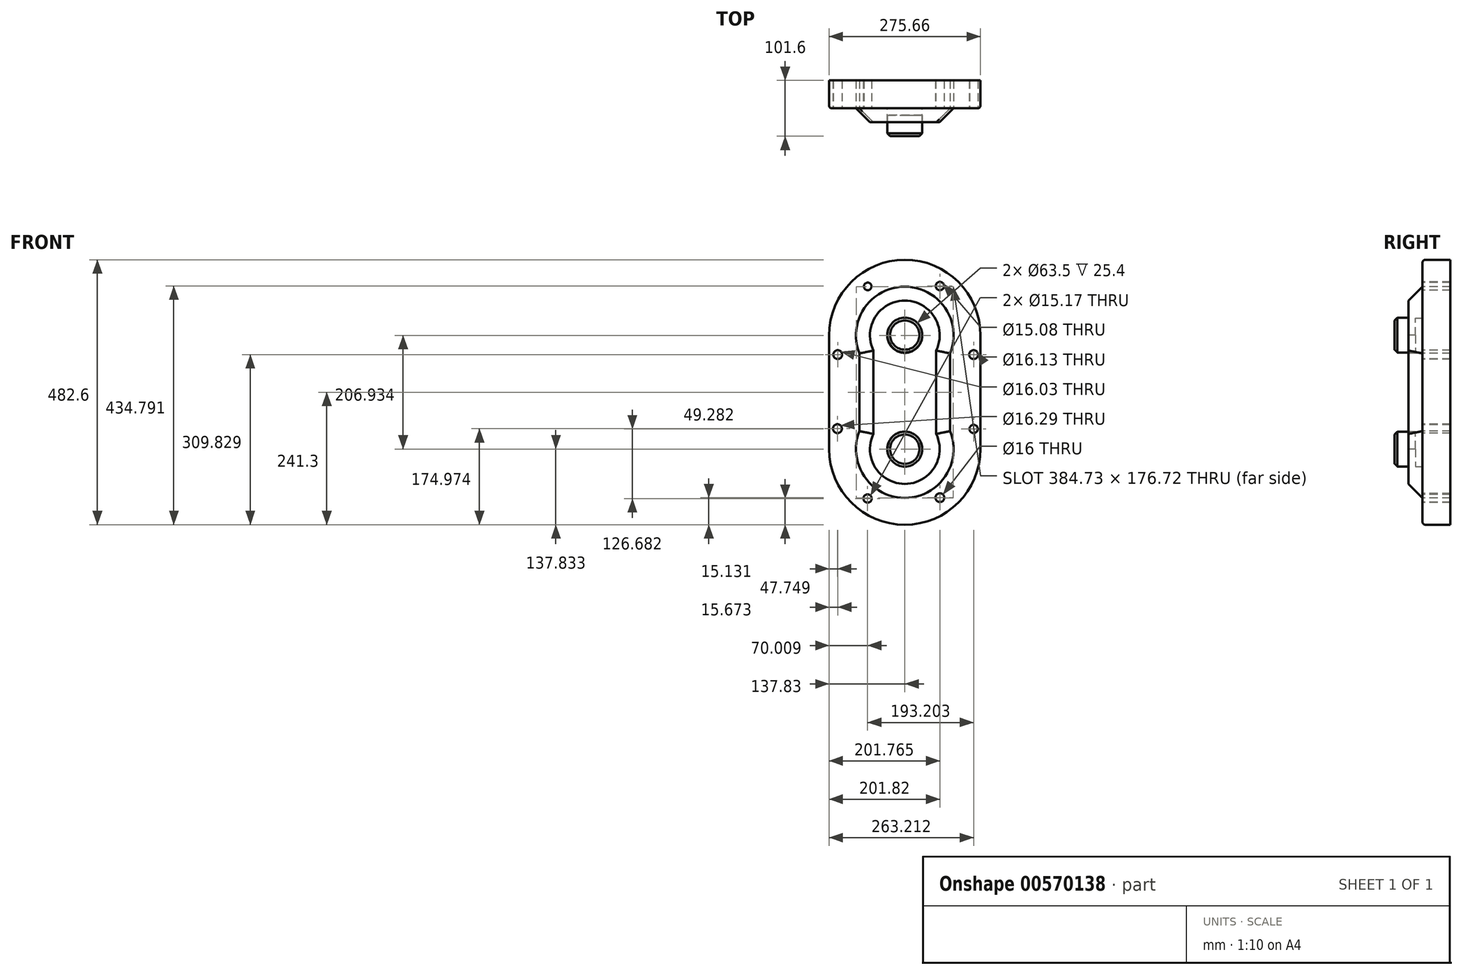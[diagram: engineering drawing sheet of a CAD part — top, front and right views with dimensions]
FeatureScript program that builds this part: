
annotation { "Feature Type Name" : "Feature", "Feature Type Description" : "" }
export const myFeature = defineFeature(function(context is Context, id is Id, definition is map)
    precondition{}
    {
        {
            var Q0;
            Q0=qCreatedBy(makeId("Front.planeOp"),FACE);
            var sketch = newSketch(context, id + "F0", { "sketchPlane" : qUnion([Q0])});
            skArc(sketch, "E0", {"start": v(137.83, 103.47) * mm, "mid": v(0, 241.3) * mm, "end": v(-137.83, 103.47) * mm});
            skArc(sketch, "E1", {"start": v(-137.83, -103.47) * mm, "mid": v(0, -241.3) * mm, "end": v(137.83, -103.47) * mm});
            skLineSegment(sketch, "E2", {"start": v(-137.83, 103.47) * mm, "end": v(-137.83, -103.47) * mm});
            skLineSegment(sketch, "E3", {"start": v(137.83, 103.47) * mm, "end": v(137.83, -103.47) * mm});
            skArc(sketch, "E4", {"start": v(82.68, 70.8) * mm, "mid": v(0, 192.37) * mm, "end": v(-82.68, 70.8) * mm});
            skArc(sketch, "E5", {"start": v(-82.68, -70.8) * mm, "mid": v(0, -192.37) * mm, "end": v(82.68, -70.8) * mm});
            skLineSegment(sketch, "E6", {"start": v(-82.68, 70.8) * mm, "end": v(-82.68, -70.8) * mm});
            skLineSegment(sketch, "E7", {"start": v(82.68, 70.8) * mm, "end": v(82.68, -70.8) * mm});
            skCircle(sketch, "E8", {"center": v(0, 103.47) * mm, "radius": 38.1 * mm});
            skCircle(sketch, "E9", {"center": v(0, -103.47) * mm, "radius": 38.1 * mm});
            skCircle(sketch, "E10", {"center": v(0, -103.47) * mm, "radius": 31.75 * mm});
            skCircle(sketch, "E11", {"center": v(0, 103.47) * mm, "radius": 31.75 * mm});
            skPoint(sketch, "E12.centerSnap0", {"position": v(0.76, 191.04) * mm});
            skPoint(sketch, "E13.centerSnap0", {"position": v(0.76, -179.65) * mm});
            skCircle(sketch, "E14", {"center": v(-67.54, 192.74) * mm, "radius": 6.93 * mm});
            skCircle(sketch, "E15", {"center": v(63.99, 193.5) * mm, "radius": 7.54 * mm});
            skCircle(sketch, "E16", {"center": v(125.38, 68.53) * mm, "radius": 8.07 * mm});
            skCircle(sketch, "E17", {"center": v(125.38, -66.87) * mm, "radius": 7.58 * mm});
            skCircle(sketch, "E18", {"center": v(-122.16, 68.53) * mm, "radius": 8.01 * mm});
            skCircle(sketch, "E19", {"center": v(-122.7, -66.33) * mm, "radius": 8.14 * mm});
            skCircle(sketch, "E20", {"center": v(-67.82, -193.55) * mm, "radius": 7.58 * mm});
            skCircle(sketch, "E21", {"center": v(63.94, -192.02) * mm, "radius": 8 * mm});
            skSolve(sketch);
        }
        {
            var Q0;
            Q0=makeQuery(id+"F0.imprint","IMPRINT",FACE,{"disambiguationData":[TD([[makeQuery(id+"F0.imprint","IMPRINT",EDGE,{"derivedFrom":sQuery(id+"F0.wireOp",EDGE,"E0")}),1.0]])]});
            extrude(context, id + "F1", {"entities" : qUnion([Q0]), "oppositeDirection" : true, "depth" : 50.8 * mm, "offsetDistance" : 25.4 * mm});
        }
        {
            var Q0;
            Q0=makeQuery(id+"F0.imprint","IMPRINT",FACE,{"disambiguationData":[TD([[makeQuery(id+"F0.imprint","IMPRINT",EDGE,{"derivedFrom":sQuery(id+"F0.wireOp",EDGE,"E8")}),1.0]])]});
            var Q1;
            Q1=makeQuery(id+"F0.imprint","IMPRINT",FACE,{"disambiguationData":[TD([[makeQuery(id+"F0.imprint","IMPRINT",EDGE,{"derivedFrom":sQuery(id+"F0.wireOp",EDGE,"E9")}),1.0]])]});
            var Q2;
            Q2=makeQuery(id+"F0.imprint","IMPRINT",FACE,{"disambiguationData":[TD([[makeQuery(id+"F0.imprint","IMPRINT",EDGE,{"derivedFrom":sQuery(id+"F0.wireOp",EDGE,"E4")}),1.0]])]});
            extrude(context, id + "F2", {"entities" : qUnion([Q0, Q1, Q2]), "depth" : 25.4 * mm, "offsetDistance" : 25.4 * mm});
        }
        {
            var Q0;
            Q0=makeQuery(id+"F2.opExtrude","CAP_FACE",FACE,{"disambiguationData":[OSD([sQuery(id+"F0.wireOp",EDGE,"E4"),sQuery(id+"F0.wireOp",EDGE,"E5"),sQuery(id+"F0.wireOp",EDGE,"E6"),sQuery(id+"F0.wireOp",EDGE,"E7"),sQuery(id+"F0.wireOp",EDGE,"E10"),sQuery(id+"F0.wireOp",EDGE,"E11")])],"isStart":false});
            cPlane(context, id + "F3", {"entities" : qUnion([Q0]), "cplaneType" : CPlaneType.OFFSET, "offset" : 25.4 * mm, "width" : 152.4 * mm, "height" : 152.4 * mm});
        }
        {
            var Q0;
            Q0=qCreatedBy(id+"F3.planeOp",FACE);
            var sketch = newSketch(context, id + "F4", { "sketchPlane" : qUnion([Q0])});
            skCircle(sketch, "E22", {"center": v(0, 104.15) * mm, "radius": 31.75 * mm});
            skCircle(sketch, "E23", {"center": v(0, -103.57) * mm, "radius": 31.75 * mm});
            skSolve(sketch);
        }
        {
            var Q0;
            Q0=makeQuery(id+"F4.imprint","IMPRINT",FACE,{"disambiguationData":[TD([[makeQuery(id+"F4.imprint","IMPRINT",EDGE,{"derivedFrom":sQuery(id+"F4.wireOp",EDGE,"E22")}),1.0]])]});
            var Q1;
            Q1=makeQuery(id+"F4.imprint","IMPRINT",FACE,{"disambiguationData":[TD([[makeQuery(id+"F4.imprint","IMPRINT",EDGE,{"derivedFrom":sQuery(id+"F4.wireOp",EDGE,"E23")}),1.0]])]});
            extrude(context, id + "F5", {"entities" : qUnion([Q0, Q1]), "operationType" : NewBodyOperationType.ADD, "oppositeDirection" : true, "depth" : 38.1 * mm, "offsetDistance" : 25.4 * mm});
        }
        {
            var Q0;
            Q0=makeQuery(id+"F5.opExtrude","CAP_EDGE",EDGE,{"disambiguationData":[OSD([sQuery(id+"F4.wireOp",EDGE,"E22")])],"isStart":true});
            var Q1;
            Q1=makeQuery(id+"F5.opExtrude","CAP_EDGE",EDGE,{"disambiguationData":[OSD([sQuery(id+"F4.wireOp",EDGE,"E23")])],"isStart":true});
            chamfer(context, id + "F6", {"entities" : qUnion([Q0, Q1]), "width" : 5.08 * mm, "tangentPropagation" : true});
        }
        {
            var Q0;
            Q0=makeQuery(id+"F1.opExtrude","CAP_EDGE",EDGE,{"disambiguationData":[OSD([sQuery(id+"F0.wireOp",EDGE,"E0")])],"isStart":true});
            fillet(context, id + "F7", {"entities" : qUnion([Q0]), "radius" : 5.08 * mm, "tangentPropagation" : true, "allowEdgeOverflow" : false});
        }
        {
            var Q0;
            Q0=makeQuery(id+"F2.opExtrude","CAP_EDGE",EDGE,{"disambiguationData":[OSD([sQuery(id+"F0.wireOp",EDGE,"E4")])],"isStart":false});
            var Q1;
            Q1=makeQuery(id+"F2.opExtrude","CAP_EDGE",EDGE,{"disambiguationData":[OSD([sQuery(id+"F0.wireOp",EDGE,"E7")])],"isStart":false});
            var Q2;
            Q2=makeQuery(id+"F2.opExtrude","CAP_EDGE",EDGE,{"disambiguationData":[OSD([sQuery(id+"F0.wireOp",EDGE,"E6")])],"isStart":false});
            var Q3;
            Q3=makeQuery(id+"F2.opExtrude","CAP_EDGE",EDGE,{"disambiguationData":[OSD([sQuery(id+"F0.wireOp",EDGE,"E5")])],"isStart":false});
            chamfer(context, id + "F8", {"entities" : qUnion([Q0, Q1, Q2, Q3]), "width" : 25.4 * mm, "tangentPropagation" : true});
        }
    });
